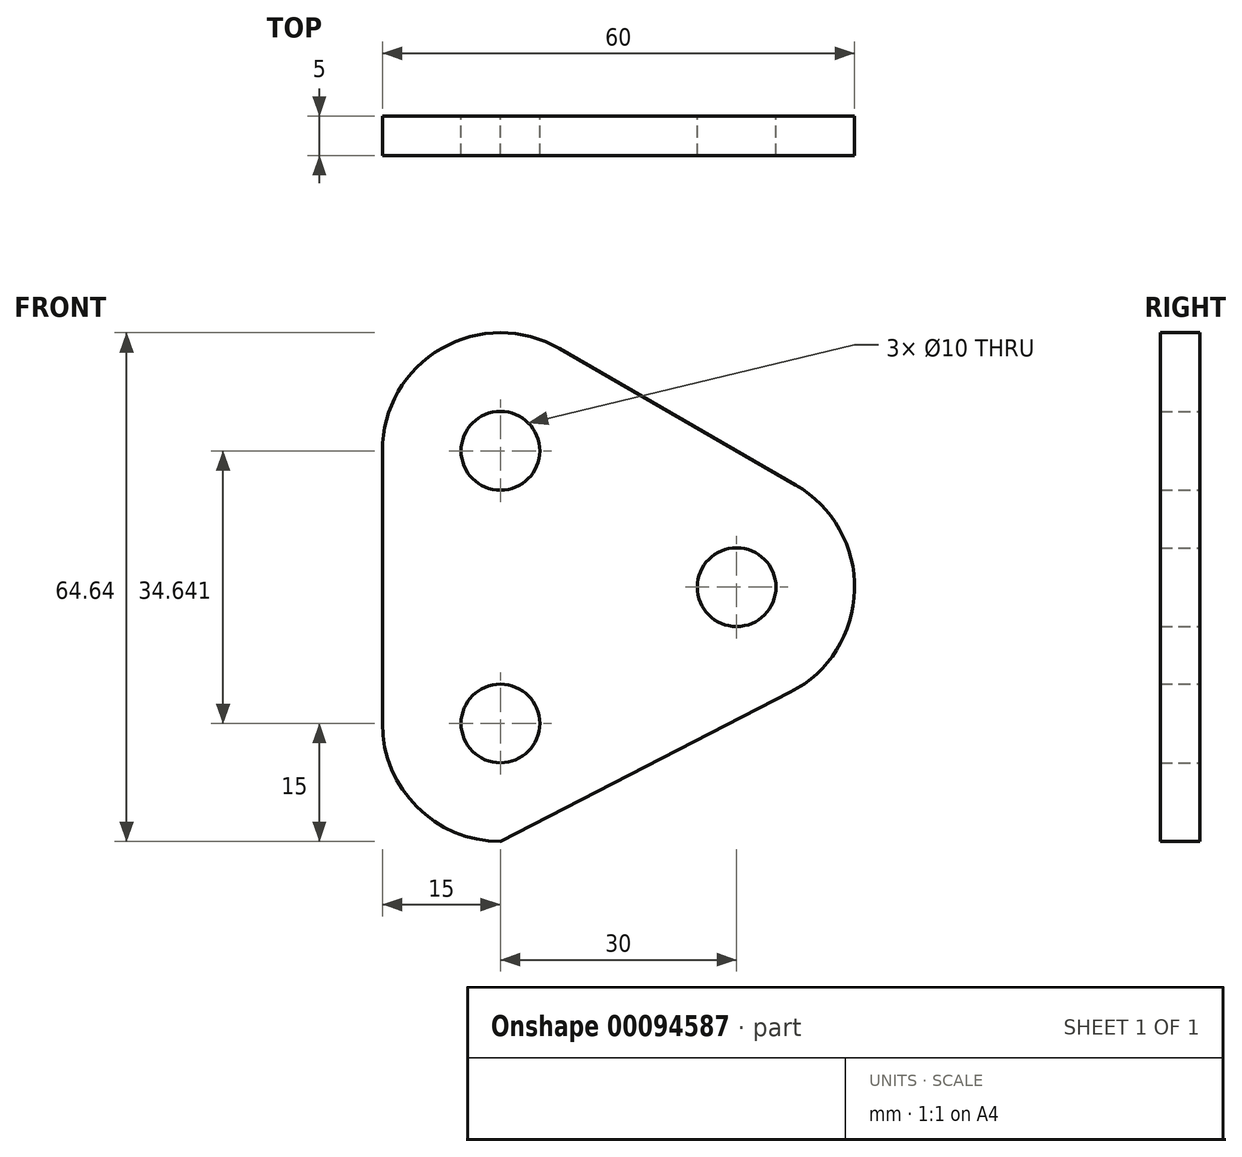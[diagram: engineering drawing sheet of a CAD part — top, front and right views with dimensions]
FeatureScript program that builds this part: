
annotation { "Feature Type Name" : "Feature", "Feature Type Description" : "" }
export const myFeature = defineFeature(function(context is Context, id is Id, definition is map)
    precondition{}
    {
        {
            var Q0;
            Q0=qCreatedBy(makeId("Front.planeOp"),FACE);
            var sketch = newSketch(context, id + "F0", { "sketchPlane" : qUnion([Q0])});
            skLineSegment(sketch, "E0", {"start": v(0, 40.22) * mm, "end": v(0, -36.52) * mm, "construction": true});
            skLineSegment(sketch, "E1", {"start": v(69.34, 0) * mm, "end": v(-51.05, 0) * mm, "construction": true});
            skCircle(sketch, "E2", {"center": v(0, 0) * mm, "radius": 20 * mm, "construction": true});
            skCircle(sketch, "E3", {"center": v(20, 0) * mm, "radius": 5 * mm});
            skCircle(sketch, "E4.1.0", {"center": v(-10, 17.32) * mm, "radius": 5 * mm});
            skCircle(sketch, "E4.2.0", {"center": v(-10, -17.32) * mm, "radius": 5 * mm});
            skArc(sketch, "E5", {"start": v(27.5, 13) * mm, "mid": v(35, -0.36) * mm, "end": v(26.87, -13.34) * mm});
            skArc(sketch, "E6", {"start": v(-10, -32.32) * mm, "mid": v(-20.6, -27.93) * mm, "end": v(-25, -17.32) * mm});
            skArc(sketch, "E7", {"start": v(-25, 17.32) * mm, "mid": v(-17.5, 30.31) * mm, "end": v(-2.5, 30.31) * mm});
            skLineSegment(sketch, "E8", {"start": v(-2.5, 30.31) * mm, "end": v(27.5, 13) * mm});
            skLineSegment(sketch, "E9", {"start": v(26.87, -13.34) * mm, "end": v(-10, -32.32) * mm});
            skLineSegment(sketch, "E10", {"start": v(-25, -17.32) * mm, "end": v(-25, 17.32) * mm});
            skSolve(sketch);
        }
        {
            var Q0;
            Q0 = qSketchRegion(id + "F0", true);
            extrude(context, id + "F1", {"entities" : qUnion([Q0]), "depth" : 5 * mm});
        }
    });
